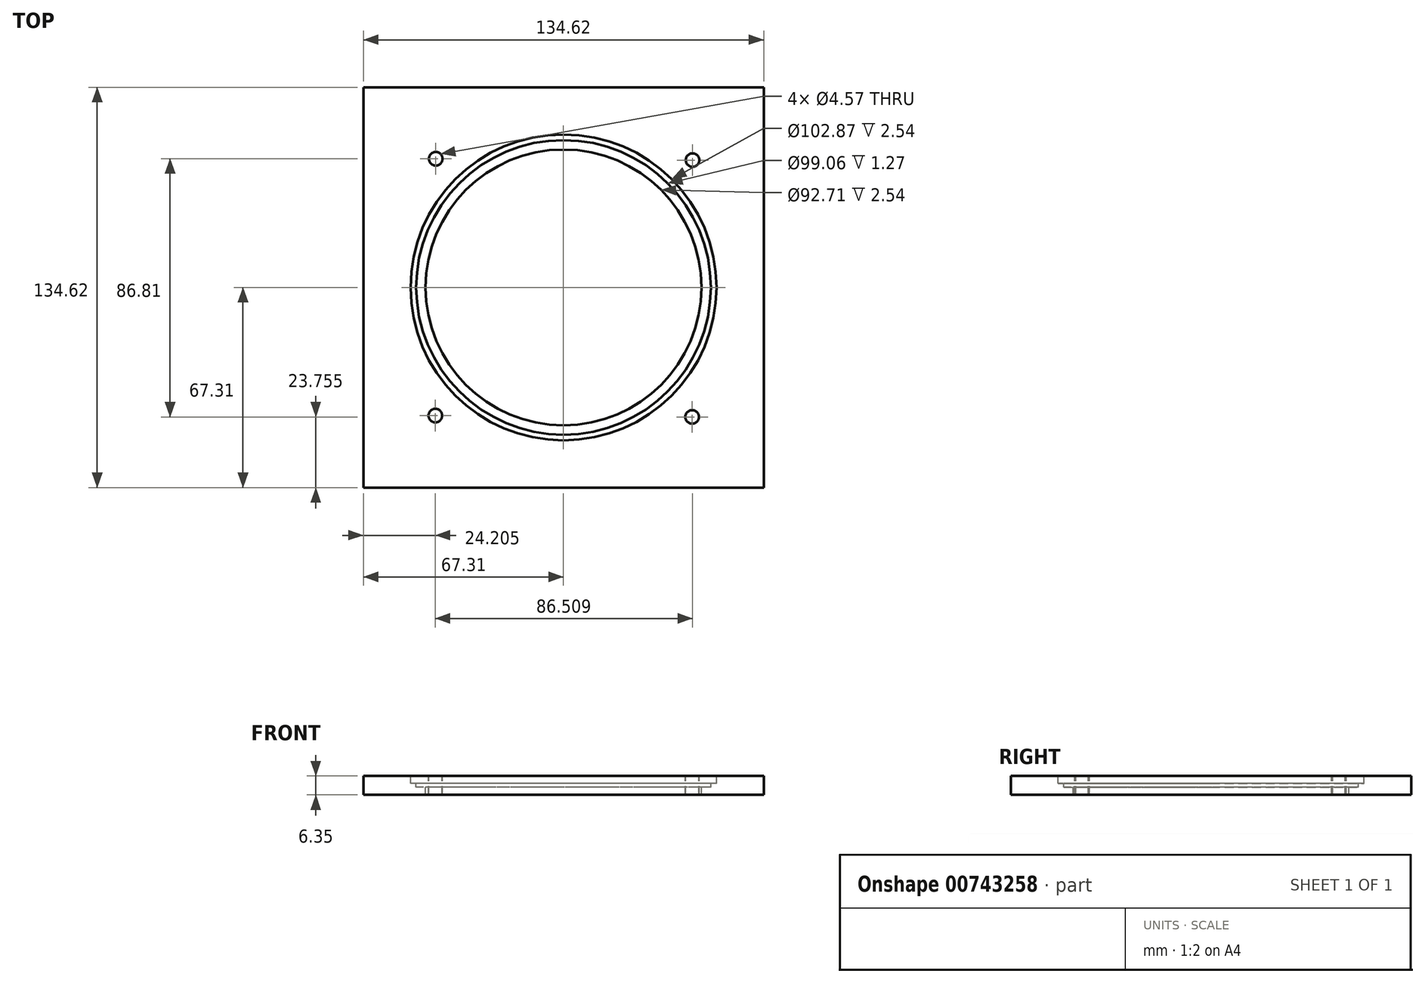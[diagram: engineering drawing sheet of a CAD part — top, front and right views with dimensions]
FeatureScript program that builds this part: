
annotation { "Feature Type Name" : "Feature", "Feature Type Description" : "" }
export const myFeature = defineFeature(function(context is Context, id is Id, definition is map)
    precondition{}
    {
        {
            var Q0;
            Q0=qCreatedBy(makeId("Top.planeOp"),FACE);
            var sketch = newSketch(context, id + "F0", { "sketchPlane" : qUnion([Q0])});
            skCircle(sketch, "E0", {"center": v(0, 0) * mm, "radius": 51.44 * mm});
            skCircle(sketch, "E1", {"center": v(-42.96, 43.25) * mm, "radius": 2.29 * mm});
            skCircle(sketch, "E2", {"center": v(-43.1, -43.1) * mm, "radius": 2.29 * mm});
            skCircle(sketch, "E3", {"center": v(43.25, -43.56) * mm, "radius": 2.29 * mm});
            skCircle(sketch, "E4", {"center": v(43.4, 42.8) * mm, "radius": 2.29 * mm});
            skLineSegment(sketch, "E5.bottom", {"start": v(-67.31, 67.31) * mm, "end": v(67.31, 67.31) * mm});
            skLineSegment(sketch, "E5.top", {"start": v(-67.31, -67.3) * mm, "end": v(67.31, -67.3) * mm});
            skLineSegment(sketch, "E5.left", {"start": v(-67.31, 67.31) * mm, "end": v(-67.31, -67.31) * mm});
            skLineSegment(sketch, "E5.right", {"start": v(67.31, 67.31) * mm, "end": v(67.31, -67.31) * mm});
            skSolve(sketch);
        }
        {
            var Q0;
            Q0=makeQuery(id+"F0.imprint","IMPRINT",FACE,{"disambiguationData":[TD([[makeQuery(id+"F0.imprint","IMPRINT",EDGE,{"derivedFrom":sQuery(id+"F0.wireOp",EDGE,"E0")}),-1.0]])]});
            cPlane(context, id + "F1", {"entities" : qUnion([Q0]), "cplaneType" : CPlaneType.OFFSET, "offset" : 2.54 * mm, "oppositeDirection" : true, "width" : 152.4 * mm, "height" : 152.4 * mm});
        }
        {
            var Q0;
            Q0=qCreatedBy(id+"F1.planeOp",FACE);
            var sketch = newSketch(context, id + "F2", { "sketchPlane" : qUnion([Q0])});
            skCircle(sketch, "E6", {"center": v(0, 0) * mm, "radius": 49.53 * mm});
            skCircle(sketch, "E7", {"center": v(-42.96, 43.25) * mm, "radius": 2.29 * mm});
            skCircle(sketch, "E8", {"center": v(-43.1, -43.1) * mm, "radius": 2.29 * mm});
            skCircle(sketch, "E9", {"center": v(43.25, -43.56) * mm, "radius": 2.29 * mm});
            skCircle(sketch, "E10", {"center": v(43.4, 42.8) * mm, "radius": 2.29 * mm});
            skLineSegment(sketch, "E11.bottom", {"start": v(-67.31, 67.31) * mm, "end": v(67.31, 67.31) * mm});
            skLineSegment(sketch, "E11.top", {"start": v(-67.31, -67.3) * mm, "end": v(67.31, -67.3) * mm});
            skLineSegment(sketch, "E11.left", {"start": v(-67.31, 67.31) * mm, "end": v(-67.31, -67.31) * mm});
            skLineSegment(sketch, "E11.right", {"start": v(67.31, 67.31) * mm, "end": v(67.31, -67.31) * mm});
            skPoint(sketch, "E12.middle", {"position": v(0, -50.8) * mm});
            skSolve(sketch);
        }
        {
            var Q0;
            Q0=makeQuery(id+"F2.imprint","IMPRINT",FACE,{"disambiguationData":[TD([[makeQuery(id+"F2.imprint","IMPRINT",EDGE,{"derivedFrom":sQuery(id+"F2.wireOp",EDGE,"E6")}),1.0]])]});
            var Q1;
            Q1=makeQuery(id+"F0.imprint","IMPRINT",FACE,{"disambiguationData":[TD([[makeQuery(id+"F0.imprint","IMPRINT",EDGE,{"derivedFrom":sQuery(id+"F0.wireOp",EDGE,"E0")}),1.0]])]});
            var Q2;
            Q2=sQuery(id+"F0.wireOp",EDGE,"E0");
            var Q3;
            Q3=sQuery(id+"F2.wireOp",EDGE,"E6");
            loft(context, id + "F3", {"bodyType" : ToolBodyType.SURFACE, "sheetProfilesArray" : [{ "sheetProfileEntities" : qUnion([Q0]) }, { "sheetProfileEntities" : qUnion([Q1]) }], "wireProfilesArray" : [{ "wireProfileEntities" : qUnion([Q2]) }, { "wireProfileEntities" : qUnion([Q3]) }]});
        }
        {
            var Q0;
            Q0 = qSketchRegion(id + "F0", true);
            extrude(context, id + "F4", {"entities" : qUnion([Q0]), "oppositeDirection" : true, "depth" : 6.35 * mm, "offsetDistance" : 25.4 * mm});
        }
        {
            var Q0;
            Q0=qCreatedBy(id+"F1.planeOp",FACE);
            cPlane(context, id + "F5", {"entities" : qUnion([Q0]), "cplaneType" : CPlaneType.OFFSET, "offset" : 1.27 * mm, "oppositeDirection" : true, "width" : 152.4 * mm, "height" : 152.4 * mm});
        }
        {
            var Q0;
            Q0=qCreatedBy(id+"F5.planeOp",FACE);
            var sketch = newSketch(context, id + "F6", { "sketchPlane" : qUnion([Q0])});
            skCircle(sketch, "E13", {"center": v(0, 0) * mm, "radius": 46.35 * mm});
            skCircle(sketch, "E14", {"center": v(-42.96, 43.25) * mm, "radius": 2.29 * mm});
            skCircle(sketch, "E15", {"center": v(-43.1, -43.1) * mm, "radius": 2.29 * mm});
            skCircle(sketch, "E16", {"center": v(43.25, -43.56) * mm, "radius": 2.29 * mm});
            skCircle(sketch, "E17", {"center": v(43.4, 42.8) * mm, "radius": 2.29 * mm});
            skLineSegment(sketch, "E18.bottom", {"start": v(-67.3, 67.3) * mm, "end": v(67.31, 67.3) * mm});
            skLineSegment(sketch, "E18.top", {"start": v(-67.31, -67.31) * mm, "end": v(67.3, -67.31) * mm});
            skLineSegment(sketch, "E18.left", {"start": v(-67.3, 67.3) * mm, "end": v(-67.31, -67.3) * mm});
            skLineSegment(sketch, "E18.right", {"start": v(67.31, 67.3) * mm, "end": v(67.3, -67.3) * mm});
            skSolve(sketch);
        }
        {
            var Q0;
            Q0 = qSketchRegion(id + "F2", true);
            extrude(context, id + "F7", {"entities" : qUnion([Q0]), "operationType" : NewBodyOperationType.ADD, "oppositeDirection" : true, "depth" : 3.8 * mm, "offsetDistance" : 25.4 * mm});
        }
        {
            var Q0;
            Q0 = qSketchRegion(id + "F6", true);
            extrude(context, id + "F8", {"entities" : qUnion([Q0]), "operationType" : NewBodyOperationType.ADD, "oppositeDirection" : true, "depth" : 2.54 * mm, "offsetDistance" : 25.4 * mm});
        }
    });
